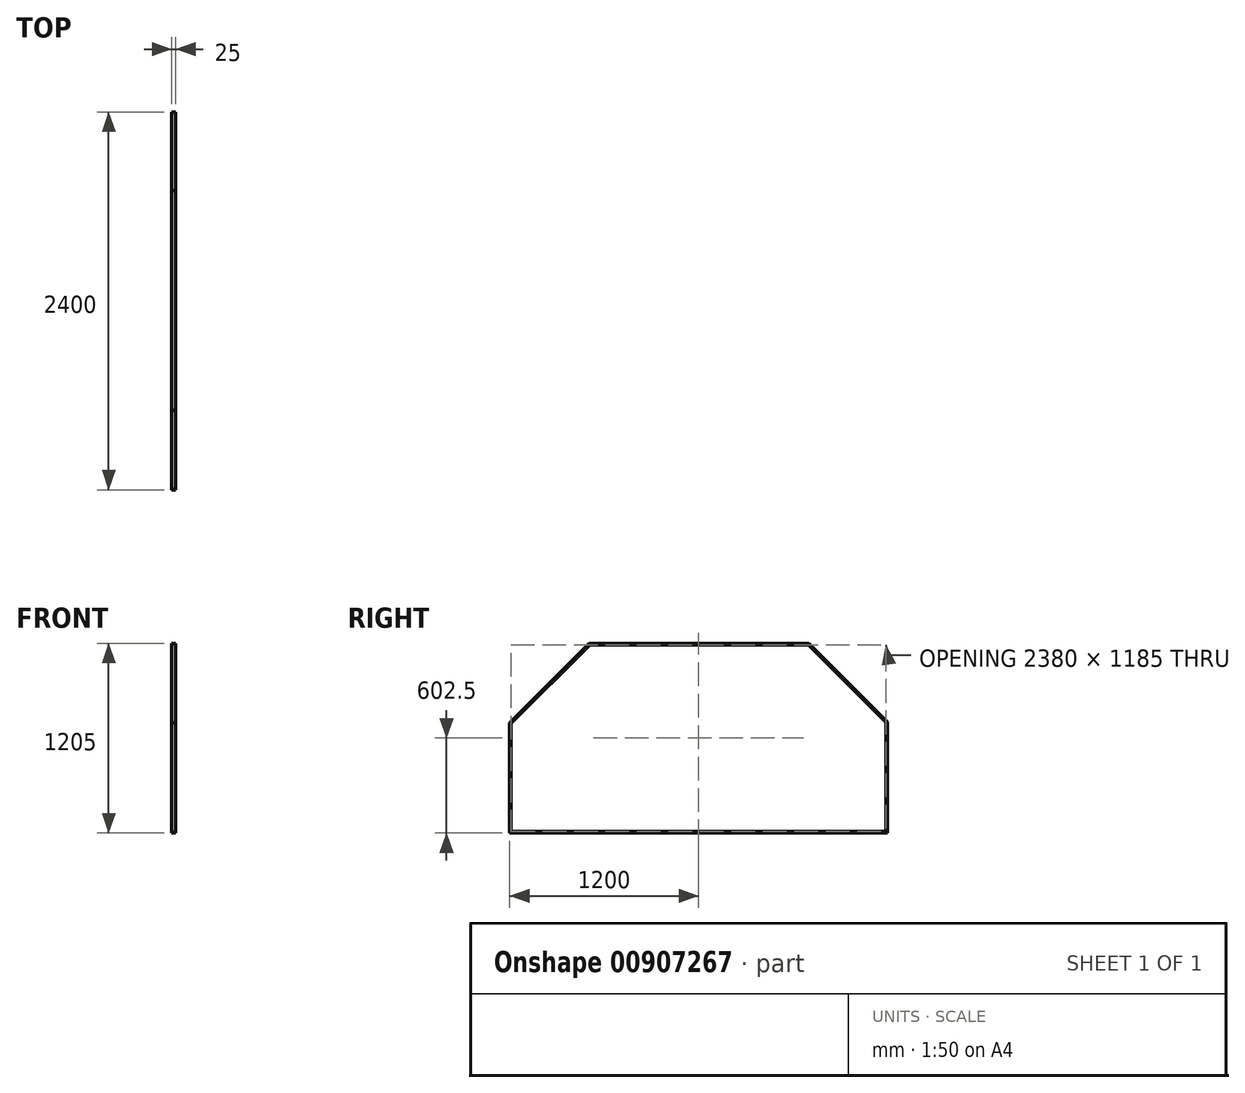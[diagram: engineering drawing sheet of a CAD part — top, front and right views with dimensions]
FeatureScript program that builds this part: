
annotation { "Feature Type Name" : "Feature", "Feature Type Description" : "" }
export const myFeature = defineFeature(function(context is Context, id is Id, definition is map)
    precondition{}
    {
        {
            var Q0;
            Q0=qCreatedBy(makeId("Right.planeOp"),FACE);
            var sketch = newSketch(context, id + "F0", { "sketchPlane" : qUnion([Q0])});
            skLineSegment(sketch, "E0.bottom", {"start": v(0, 0) * mm, "end": v(2400, 0) * mm});
            skLineSegment(sketch, "E0.top", {"start": v(505, 1205) * mm, "end": v(1902.07, 1205) * mm});
            skLineSegment(sketch, "E0.left", {"start": v(0, 0) * mm, "end": v(0, 700) * mm});
            skLineSegment(sketch, "E0.right", {"start": v(2400, 0) * mm, "end": v(2400, 707.07) * mm});
            skLineSegment(sketch, "E1", {"start": v(0, 700) * mm, "end": v(505, 1205) * mm});
            skLineSegment(sketch, "E2", {"start": v(2400, 707.07) * mm, "end": v(1902.07, 1205) * mm});
            skLineSegment(sketch, "E3.0", {"start": v(10, 695.86) * mm, "end": v(509.14, 1195) * mm});
            skLineSegment(sketch, "E3.1", {"start": v(2390, 702.93) * mm, "end": v(1897.93, 1195) * mm});
            skLineSegment(sketch, "E3.2", {"start": v(2390, 10) * mm, "end": v(2390, 702.93) * mm});
            skLineSegment(sketch, "E3.3", {"start": v(509.14, 1195) * mm, "end": v(1897.93, 1195) * mm});
            skLineSegment(sketch, "E3.4", {"start": v(10, 10) * mm, "end": v(2390, 10) * mm});
            skLineSegment(sketch, "E3.5", {"start": v(10, 10) * mm, "end": v(10, 695.86) * mm});
            skSolve(sketch);
        }
        {
            var Q0;
            Q0=makeQuery(id+"F0.imprint","IMPRINT",FACE,{"disambiguationData":[TD([[makeQuery(id+"F0.imprint","IMPRINT",EDGE,{"derivedFrom":sQuery(id+"F0.wireOp",EDGE,"E0.bottom")}),1.0]])]});
            extrude(context, id + "F1", {"entities" : qUnion([Q0]), "endBound" : BoundingType.SYMMETRIC, "depth" : 25 * mm, "offsetDistance" : 25 * mm});
        }
    });
